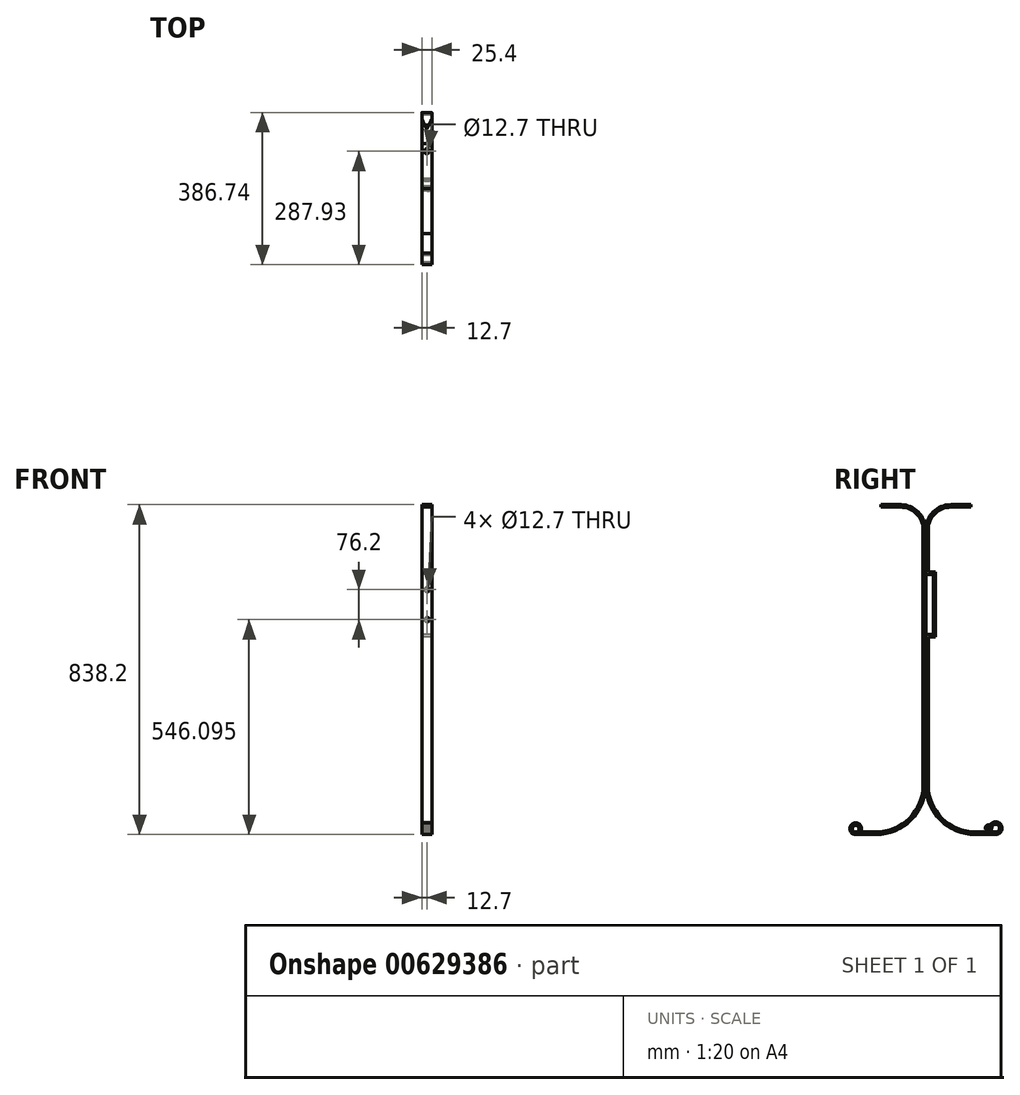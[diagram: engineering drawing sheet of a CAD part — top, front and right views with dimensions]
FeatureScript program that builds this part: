
annotation { "Feature Type Name" : "Feature", "Feature Type Description" : "" }
export const myFeature = defineFeature(function(context is Context, id is Id, definition is map)
    precondition{}
    {
        {
            var Q0;
            Q0=qCreatedBy(makeId("Right.planeOp"),FACE);
            var sketch = newSketch(context, id + "F0", { "sketchPlane" : qUnion([Q0])});
            skLineSegment(sketch, "E0", {"start": v(0, -26.53) * mm, "end": v(0, -140.83) * mm});
            skLineSegment(sketch, "E1", {"start": v(63.5, 36.97) * mm, "end": v(114.3, 36.97) * mm});
            skLineSegment(sketch, "E2", {"start": v(127, -801.23) * mm, "end": v(177.8, -801.23) * mm});
            skLineSegment(sketch, "E3", {"start": v(0, -140.83) * mm, "end": v(19.05, -140.83) * mm});
            skLineSegment(sketch, "E4", {"start": v(19.05, -140.83) * mm, "end": v(19.05, -293.23) * mm});
            skLineSegment(sketch, "E5", {"start": v(19.05, -293.23) * mm, "end": v(0, -293.23) * mm});
            skPoint(sketch, "E6.visualSharp", {"position": v(0, 36.97) * mm});
            skArc(sketch, "E6.filletArc", {"start": v(6.35, 36.97) * mm, "mid": v(5, 36.82) * mm, "end": v(3.72, 36.4) * mm});
            skArc(sketch, "E7.filletArc", {"start": v(63.5, 36.97) * mm, "mid": v(18.6, 18.37) * mm, "end": v(0, -26.53) * mm});
            skArc(sketch, "E8.0", {"start": v(63.5, 30.62) * mm, "mid": v(23.09, 13.88) * mm, "end": v(6.35, -26.53) * mm});
            skLineSegment(sketch, "E9.trimOffspring", {"start": v(0, -293.23) * mm, "end": v(0, -674.23) * mm});
            skLineSegment(sketch, "E10.2", {"start": v(25.4, -299.58) * mm, "end": v(6.35, -299.58) * mm});
            skLineSegment(sketch, "E10.3", {"start": v(25.4, -134.48) * mm, "end": v(25.4, -299.58) * mm});
            skLineSegment(sketch, "E10.7", {"start": v(6.35, -134.48) * mm, "end": v(25.4, -134.48) * mm});
            skLineSegment(sketch, "E11", {"start": v(114.3, 36.97) * mm, "end": v(114.3, 30.62) * mm});
            skPoint(sketch, "E12.visualSharp", {"position": v(0, -801.23) * mm});
            skArc(sketch, "E12.filletArc", {"start": v(0, -674.23) * mm, "mid": v(37.2, -764.04) * mm, "end": v(127, -801.23) * mm});
            skPoint(sketch, "E13.visualSharp", {"position": v(6.35, -667.88) * mm});
            skLineSegment(sketch, "E14", {"start": v(63.5, 30.62) * mm, "end": v(114.3, 30.62) * mm});
            skLineSegment(sketch, "E15", {"start": v(6.35, -26.53) * mm, "end": v(6.35, -134.48) * mm});
            skLineSegment(sketch, "E16.0", {"start": v(127, -794.88) * mm, "end": v(177.8, -794.88) * mm});
            skArc(sketch, "E16.1", {"start": v(6.35, -674.23) * mm, "mid": v(41.69, -759.55) * mm, "end": v(127, -794.88) * mm});
            skLineSegment(sketch, "E16.2", {"start": v(6.35, -299.58) * mm, "end": v(6.35, -674.23) * mm});
            skArc(sketch, "E17.MirrorCS", {"start": v(-6.35, 36.97) * mm, "mid": v(-5, 36.82) * mm, "end": v(-3.72, 36.4) * mm});
            skArc(sketch, "E18.MirrorCS", {"start": v(-63.5, 36.97) * mm, "mid": v(-18.6, 18.37) * mm, "end": v(0, -26.53) * mm});
            skArc(sketch, "E19.MirrorCS", {"start": v(-63.5, 30.62) * mm, "mid": v(-23.09, 13.88) * mm, "end": v(-6.35, -26.53) * mm});
            skLineSegment(sketch, "E20.MirrorCS", {"start": v(-114.3, 36.97) * mm, "end": v(-114.3, 30.62) * mm});
            skLineSegment(sketch, "E21.MirrorCS", {"start": v(-63.5, 30.62) * mm, "end": v(-114.3, 30.62) * mm});
            skLineSegment(sketch, "E22.MirrorCS", {"start": v(-63.5, 36.97) * mm, "end": v(-114.3, 36.97) * mm});
            skLineSegment(sketch, "E23.MirrorCS", {"start": v(-127, -801.23) * mm, "end": v(-177.8, -801.23) * mm});
            skArc(sketch, "E24.MirrorCS", {"start": v(-6.35, -674.23) * mm, "mid": v(-41.69, -759.55) * mm, "end": v(-127, -794.88) * mm});
            skLineSegment(sketch, "E25.MirrorCS", {"start": v(-127, -794.88) * mm, "end": v(-177.8, -794.88) * mm});
            skPoint(sketch, "E26.MirrorP", {"position": v(-6.35, -667.88) * mm});
            skArc(sketch, "E27.MirrorCS", {"start": v(0, -674.23) * mm, "mid": v(-37.2, -764.04) * mm, "end": v(-127, -801.23) * mm});
            skLineSegment(sketch, "E28", {"start": v(0, -674.23) * mm, "end": v(0, -26.53) * mm});
            skLineSegment(sketch, "E29", {"start": v(-6.35, -674.23) * mm, "end": v(-6.35, -26.53) * mm});
            skArc(sketch, "E30.MirrorCS", {"start": v(-177.8, -794.88) * mm, "mid": v(-182.21, -779.06) * mm, "end": v(-170.25, -790.32) * mm});
            skArc(sketch, "E31.MirrorCS", {"start": v(-177.8, -801.23) * mm, "mid": v(-185.5, -773.62) * mm, "end": v(-164.62, -793.27) * mm});
            skLineSegment(sketch, "E32.MirrorCS", {"start": v(-164.62, -793.27) * mm, "end": v(-170.25, -790.32) * mm});
            skArc(sketch, "E33", {"start": v(177.8, -801.23) * mm, "mid": v(189.4, -773.57) * mm, "end": v(161.54, -784.7) * mm});
            skArc(sketch, "E34.0", {"start": v(177.8, -794.88) * mm, "mid": v(184.87, -778.02) * mm, "end": v(167.89, -784.8) * mm});
            skArc(sketch, "E35", {"start": v(167.89, -784.8) * mm, "mid": v(153.05, -789.38) * mm, "end": v(162.32, -776.92) * mm});
            skArc(sketch, "E36.0", {"start": v(161.54, -784.7) * mm, "mid": v(158.23, -785.71) * mm, "end": v(160.3, -782.94) * mm});
            skLineSegment(sketch, "E37", {"start": v(160.3, -782.94) * mm, "end": v(162.32, -776.92) * mm});
            skSolve(sketch);
        }
        {
            var Q0;
            Q0=makeQuery(id+"F0.imprint","IMPRINT",FACE,{"disambiguationData":[TD([[makeQuery(id+"F0.imprint","IMPRINT",EDGE,{"derivedFrom":sQuery(id+"F0.wireOp",EDGE,"E0")}),1.0]])]});
            extrude(context, id + "F1", {"entities" : qUnion([Q0]), "depth" : 25.4 * mm, "offsetDistance" : 25.4 * mm});
        }
        {
            var Q0;
            Q0=makeQuery(id+"F1.opExtrude","SWEPT_FACE",FACE,{"disambiguationData":[OSD([sQuery(id+"F0.wireOp",EDGE,"E10.3")])]});
            var sketch = newSketch(context, id + "F2", { "sketchPlane" : qUnion([Q0])});
            skCircle(sketch, "E38", {"center": v(-12.7, -178.93) * mm, "radius": 6.35 * mm});
            skPoint(sketch, "E38.centerSnap0", {"position": v(-12.7, -134.48) * mm});
            skCircle(sketch, "E39", {"center": v(-12.7, -255.13) * mm, "radius": 6.35 * mm});
            skPoint(sketch, "E40.0", {"position": v(-25.4, -140.83) * mm});
            skPoint(sketch, "E41.0", {"position": v(-25.4, -293.23) * mm});
            skSolve(sketch);
        }
        {
            var Q0;
            Q0=makeQuery(id+"F2.imprint","IMPRINT",FACE,{"disambiguationData":[TD([[makeQuery(id+"F2.imprint","IMPRINT",EDGE,{"derivedFrom":sQuery(id+"F2.wireOp",EDGE,"E38")}),1.0]])]});
            var Q1;
            Q1=makeQuery(id+"F2.imprint","IMPRINT",FACE,{"disambiguationData":[TD([[makeQuery(id+"F2.imprint","IMPRINT",EDGE,{"derivedFrom":sQuery(id+"F2.wireOp",EDGE,"E39")}),1.0]])]});
            extrude(context, id + "F3", {"entities" : qUnion([Q0, Q1]), "operationType" : NewBodyOperationType.REMOVE, "endBound" : BoundingType.THROUGH_ALL, "oppositeDirection" : true, "depth" : 42.93 * mm, "offsetDistance" : 25.4 * mm});
        }
        {
            var Q0;
            Q0=makeQuery(id+"F0.imprint","IMPRINT",FACE,{"disambiguationData":[TD([[makeQuery(id+"F0.imprint","IMPRINT",EDGE,{"derivedFrom":sQuery(id+"F0.wireOp",EDGE,"E0")}),-1.0]])]});
            extrude(context, id + "F4", {"entities" : qUnion([Q0]), "depth" : 25.4 * mm, "offsetDistance" : 25.4 * mm});
        }
        {
            var Q0;
            Q0=makeQuery(id+"F4.opExtrude","SWEPT_FACE",FACE,{"disambiguationData":[OSD([sQuery(id+"F0.wireOp",EDGE,"E0"),sQuery(id+"F0.wireOp",EDGE,"E9.trimOffspring"),sQuery(id+"F0.wireOp",EDGE,"E28")])]});
            var sketch = newSketch(context, id + "F5", { "sketchPlane" : qUnion([Q0])});
            skCircle(sketch, "E42.0", {"center": v(-12.7, -178.93) * mm, "radius": 6.35 * mm});
            skCircle(sketch, "E43.0", {"center": v(-12.7, -255.13) * mm, "radius": 6.35 * mm});
            skSolve(sketch);
        }
        {
            var Q0;
            Q0=makeQuery(id+"F5.imprint","IMPRINT",FACE,{"disambiguationData":[TD([[makeQuery(id+"F5.imprint","IMPRINT",EDGE,{"derivedFrom":sQuery(id+"F5.wireOp",EDGE,"E42.0")}),1.0]])]});
            var Q1;
            Q1=makeQuery(id+"F5.imprint","IMPRINT",FACE,{"disambiguationData":[TD([[makeQuery(id+"F5.imprint","IMPRINT",EDGE,{"derivedFrom":sQuery(id+"F5.wireOp",EDGE,"E43.0")}),1.0]])]});
            extrude(context, id + "F6", {"entities" : qUnion([Q0, Q1]), "operationType" : NewBodyOperationType.REMOVE, "endBound" : BoundingType.THROUGH_ALL, "oppositeDirection" : true, "depth" : 25.4 * mm, "offsetDistance" : 25.4 * mm});
        }
        {
            var Q0;
            Q0=makeQuery(id+"F1.opExtrude","SWEPT_FACE",FACE,{"disambiguationData":[OSD([sQuery(id+"F0.wireOp",EDGE,"E1")])]});
            var sketch = newSketch(context, id + "F7", { "sketchPlane" : qUnion([Q0])});
            skCircle(sketch, "E44", {"center": v(12.7, 95.25) * mm, "radius": 6.35 * mm});
            skPoint(sketch, "E44.centerSnap0", {"position": v(12.7, 114.3) * mm});
            skLineSegment(sketch, "E45.0.0", {"start": v(0, 0) * mm, "end": v(0, -63.5) * mm});
            skLineSegment(sketch, "E45.0.1", {"start": v(0, -63.5) * mm, "end": v(25.4, -63.5) * mm});
            skLineSegment(sketch, "E45.0.2", {"start": v(25.4, -63.5) * mm, "end": v(25.4, 0) * mm});
            skLineSegment(sketch, "E45.0.3", {"start": v(25.4, 0) * mm, "end": v(0, 0) * mm});
            skCircle(sketch, "E46.MirrorC", {"center": v(12.7, -95.25) * mm, "radius": 6.35 * mm});
            skSolve(sketch);
        }
        {
            var Q0;
            Q0=makeQuery(id+"F7.imprint","IMPRINT",FACE,{"disambiguationData":[TD([[makeQuery(id+"F7.imprint","IMPRINT",EDGE,{"derivedFrom":sQuery(id+"F7.wireOp",EDGE,"E44")}),1.0]])]});
            var Q1;
            Q1=makeQuery(id+"F7.imprint","IMPRINT",FACE,{"disambiguationData":[TD([[makeQuery(id+"F7.imprint","IMPRINT",EDGE,{"derivedFrom":sQuery(id+"F7.wireOp",EDGE,"E46.MirrorC")}),-1.0]])]});
            var Q2;
            Q2=makeQuery(id+"F1.opExtrude","SWEPT_FACE",FACE,{"disambiguationData":[OSD([sQuery(id+"F0.wireOp",EDGE,"E14")])]});
            extrude(context, id + "F8", {"entities" : qUnion([Q0, Q1]), "operationType" : NewBodyOperationType.REMOVE, "oppositeDirection" : true, "depth" : 25.4 * mm, "endBoundEntityFace" : qUnion([Q2]), "offsetDistance" : 25.4 * mm});
        }
        {
            var Q0;
            Q0=makeQuery(id+"F1.opExtrude","SWEPT_FACE",FACE,{"disambiguationData":[OSD([sQuery(id+"F0.wireOp",EDGE,"E16.0")])]});
            var sketch = newSketch(context, id + "F9", { "sketchPlane" : qUnion([Q0])});
            skLineSegment(sketch, "E47", {"start": v(25.4, 151.55) * mm, "end": v(0, 151.55) * mm});
            skLineSegment(sketch, "E48", {"start": v(0, 177.8) * mm, "end": v(12.7, 151.55) * mm});
            skLineSegment(sketch, "E49", {"start": v(12.7, 151.55) * mm, "end": v(25.4, 177.8) * mm});
            skLineSegment(sketch, "E50", {"start": v(0, 177.8) * mm, "end": v(0, 151.55) * mm});
            skLineSegment(sketch, "E51", {"start": v(25.4, 177.8) * mm, "end": v(25.4, 151.55) * mm});
            skSolve(sketch);
        }
        {
            var Q0;
            {var subQ2=sQuery(id+"F9.wireOp",EDGE,"E48");Q0=makeQuery(id+"F9.imprint","IMPRINT",FACE,{"disambiguationData":[TD([[makeQuery(id+"F9.imprint","IMPRINT",EDGE,{"derivedFrom":subQ2}),-1.0]])]});}
            var Q1;
            {var subQ2=sQuery(id+"F9.wireOp",EDGE,"E49");Q1=makeQuery(id+"F9.imprint","IMPRINT",FACE,{"disambiguationData":[TD([[makeQuery(id+"F9.imprint","IMPRINT",EDGE,{"derivedFrom":subQ2}),-1.0]])]});}
            extrude(context, id + "F10", {"entities" : qUnion([Q0, Q1]), "operationType" : NewBodyOperationType.REMOVE, "depth" : 37.85 * mm, "offsetDistance" : 25.4 * mm});
        }
    });
